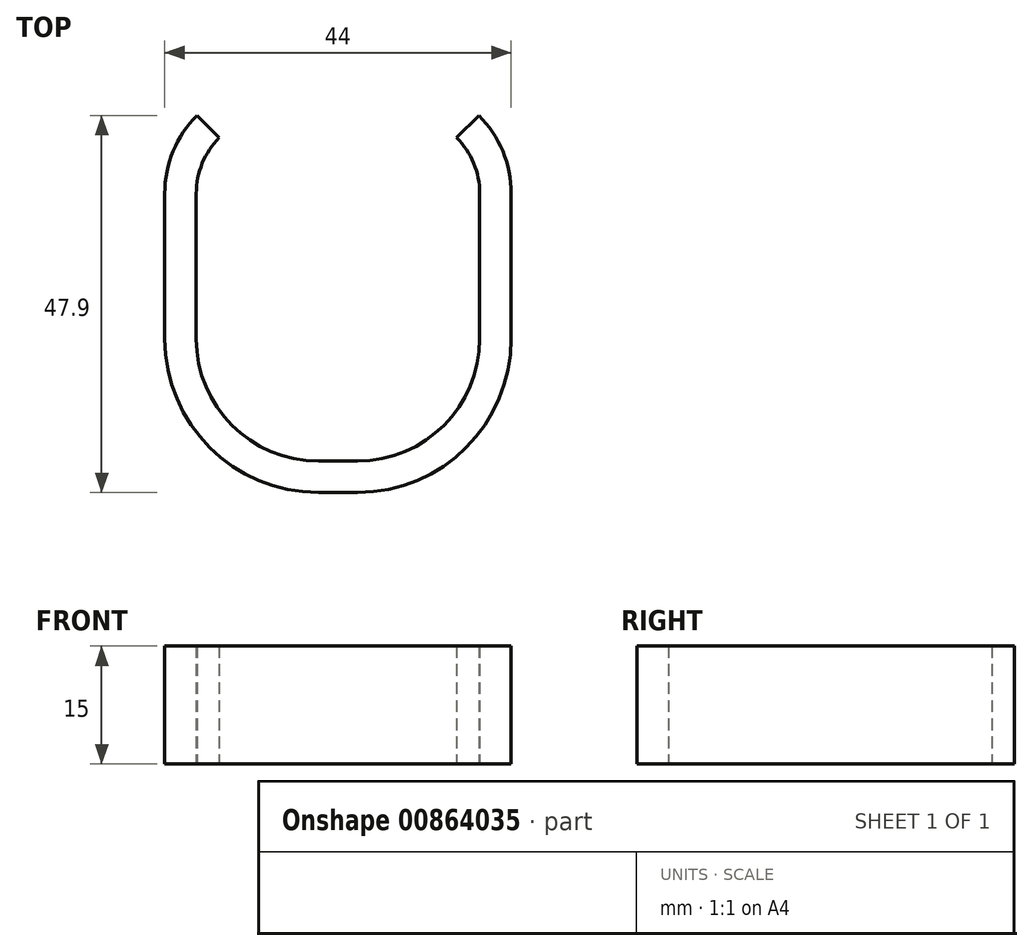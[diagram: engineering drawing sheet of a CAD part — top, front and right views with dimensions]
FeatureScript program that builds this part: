
annotation { "Feature Type Name" : "Feature", "Feature Type Description" : "" }
export const myFeature = defineFeature(function(context is Context, id is Id, definition is map)
    precondition{}
    {
        {
            var Q0;
            Q0=qCreatedBy(makeId("Top.planeOp"),FACE);
            var sketch = newSketch(context, id + "F0", { "sketchPlane" : qUnion([Q0])});
            skLineSegment(sketch, "E0.bottom", {"start": v(-8, 22) * mm, "end": v(8, 22) * mm});
            skLineSegment(sketch, "E0.top", {"start": v(-2.5, -22) * mm, "end": v(2.5, -22) * mm});
            skLineSegment(sketch, "E0.left", {"start": v(-18, 12) * mm, "end": v(-18, -6.5) * mm});
            skLineSegment(sketch, "E0.right", {"start": v(18, 12) * mm, "end": v(18, -6.5) * mm});
            skPoint(sketch, "E1.visualSharp", {"position": v(-18, -22) * mm});
            skArc(sketch, "E1.filletArc", {"start": v(-18, -6.5) * mm, "mid": v(-13.46, -17.46) * mm, "end": v(-2.5, -22) * mm});
            skArc(sketch, "E2.filletArc", {"start": v(18, 12) * mm, "mid": v(15.07, 19.07) * mm, "end": v(8, 22) * mm});
            skPoint(sketch, "E3.visualSharp", {"position": v(18, -22) * mm});
            skArc(sketch, "E3.filletArc", {"start": v(2.5, -22) * mm, "mid": v(13.46, -17.46) * mm, "end": v(18, -6.5) * mm});
            skArc(sketch, "E4.filletArc", {"start": v(-8, 22) * mm, "mid": v(-15.07, 19.07) * mm, "end": v(-18, 12) * mm});
            skLineSegment(sketch, "E5", {"start": v(-18, 12) * mm, "end": v(18, 12) * mm});
            skLineSegment(sketch, "E6", {"start": v(-8, 12) * mm, "end": v(-15.07, 19.07) * mm});
            skLineSegment(sketch, "E7", {"start": v(8, 12) * mm, "end": v(15.07, 19.07) * mm});
            skLineSegment(sketch, "E8", {"start": v(-18, 12) * mm, "end": v(-8, 12) * mm});
            skLineSegment(sketch, "E9", {"start": v(8, 12) * mm, "end": v(18, 12) * mm});
            skArc(sketch, "E10", {"start": v(-18, 12) * mm, "mid": v(-17.24, 15.83) * mm, "end": v(-15.07, 19.07) * mm});
            skArc(sketch, "E11", {"start": v(18, 12) * mm, "mid": v(17.24, 15.83) * mm, "end": v(15.07, 19.07) * mm});
            skArc(sketch, "E12.0", {"start": v(-22, 12) * mm, "mid": v(-20.93, 17.36) * mm, "end": v(-17.9, 21.9) * mm});
            skLineSegment(sketch, "E12.1", {"start": v(-22, 12) * mm, "end": v(-22, -6.5) * mm});
            skArc(sketch, "E12.2", {"start": v(-22, -6.5) * mm, "mid": v(-16.29, -20.29) * mm, "end": v(-2.5, -26) * mm});
            skArc(sketch, "E12.3", {"start": v(22, 12) * mm, "mid": v(20.93, 17.36) * mm, "end": v(17.9, 21.9) * mm});
            skLineSegment(sketch, "E12.4", {"start": v(22, 12) * mm, "end": v(22, -6.5) * mm});
            skArc(sketch, "E12.5", {"start": v(2.5, -26) * mm, "mid": v(16.29, -20.29) * mm, "end": v(22, -6.5) * mm});
            skLineSegment(sketch, "E12.6", {"start": v(-2.5, -26) * mm, "end": v(2.5, -26) * mm});
            skLineSegment(sketch, "E13", {"start": v(-17.9, 21.9) * mm, "end": v(-15.07, 19.07) * mm});
            skLineSegment(sketch, "E14", {"start": v(15.07, 19.07) * mm, "end": v(17.9, 21.9) * mm});
            skSolve(sketch);
        }
        {
            var Q0;
            Q0=makeQuery(id+"F0.imprint","IMPRINT",FACE,{"disambiguationData":[TD([[makeQuery(id+"F0.imprint","IMPRINT",EDGE,{"derivedFrom":sQuery(id+"F0.wireOp",EDGE,"E0.top")}),-1.0]])]});
            extrude(context, id + "F1", {"entities" : qUnion([Q0]), "depth" : 15 * mm, "offsetDistance" : 25 * mm});
        }
    });
